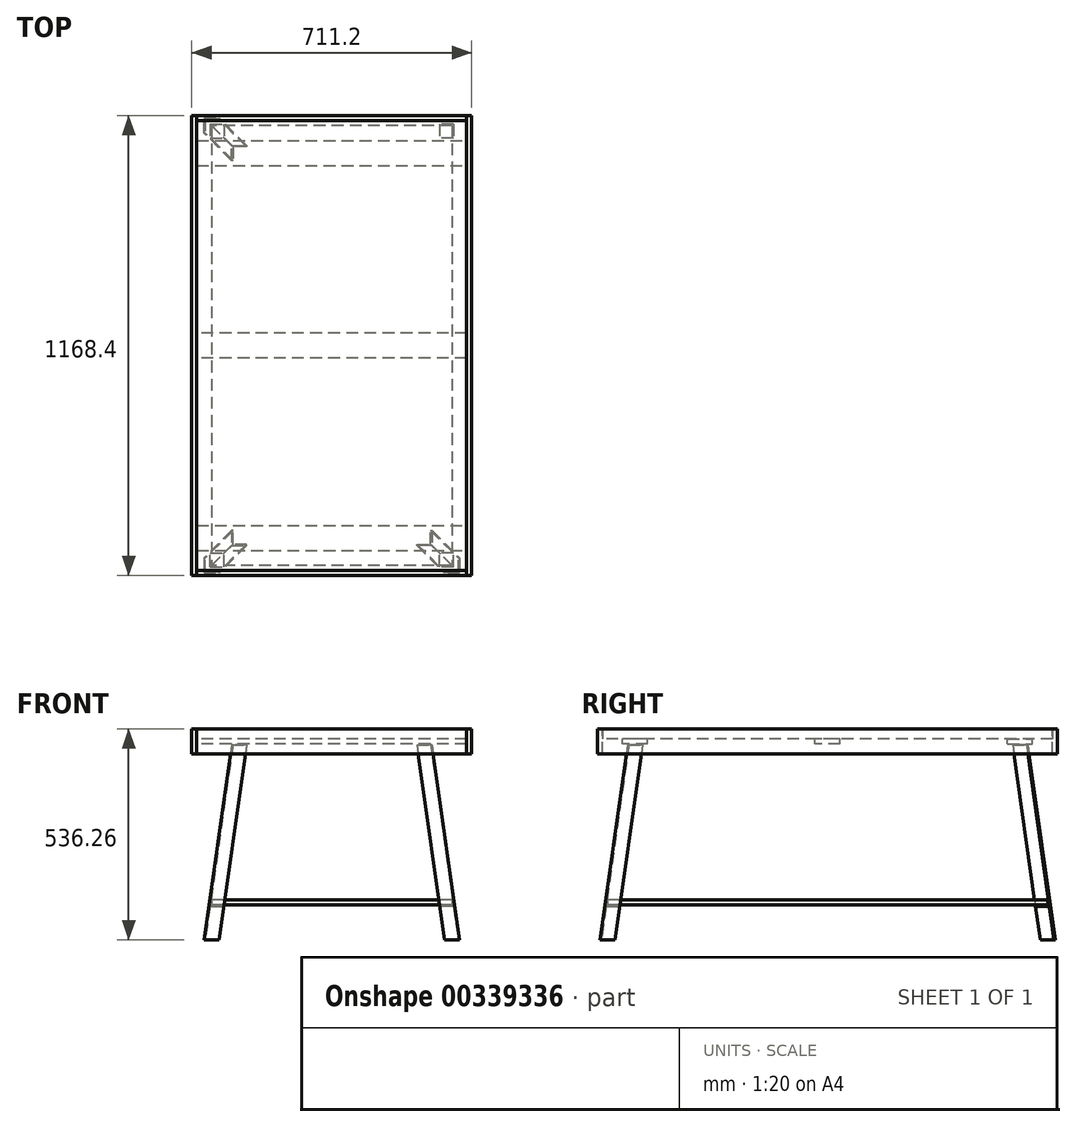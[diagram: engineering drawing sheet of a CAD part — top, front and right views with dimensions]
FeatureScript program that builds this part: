
annotation { "Feature Type Name" : "Feature", "Feature Type Description" : "" }
export const myFeature = defineFeature(function(context is Context, id is Id, definition is map)
    precondition{}
    {
        {
            var Q0;
            Q0=qCreatedBy(makeId("Top.planeOp"),FACE);
            var sketch = newSketch(context, id + "F0", { "sketchPlane" : qUnion([Q0])});
            skLineSegment(sketch, "E0.bottom", {"start": v(342.9, 571.5) * mm, "end": v(-342.9, 571.5) * mm});
            skLineSegment(sketch, "E0.top", {"start": v(342.9, -571.5) * mm, "end": v(-342.9, -571.5) * mm});
            skLineSegment(sketch, "E0.left", {"start": v(342.9, 571.5) * mm, "end": v(342.9, -571.5) * mm});
            skLineSegment(sketch, "E0.right", {"start": v(-342.9, 571.5) * mm, "end": v(-342.9, -571.5) * mm});
            skPoint(sketch, "E0.middle", {"position": v(0, 0) * mm});
            skSolve(sketch);
        }
        {
            var Q0;
            Q0=qSketchRegion(id+"F0",true);
            extrude(context, id + "F1", {"entities" : qUnion([Q0]), "depth" : 25.4 * mm});
        }
        {
            var Q0;
            Q0=makeQuery(id+"F1.opExtrude","CAP_FACE",FACE,{"disambiguationData":[OSD([sQuery(id+"F0.wireOp",EDGE,"E0.bottom"),sQuery(id+"F0.wireOp",EDGE,"E0.top"),sQuery(id+"F0.wireOp",EDGE,"E0.left"),sQuery(id+"F0.wireOp",EDGE,"E0.right")])],"isStart":false});
            var sketch = newSketch(context, id + "F2", { "sketchPlane" : qUnion([Q0])});
            skLineSegment(sketch, "E1.bottom", {"start": v(-342.9, -571.5) * mm, "end": v(342.9, -571.5) * mm});
            skLineSegment(sketch, "E1.top", {"start": v(-342.9, -584.2) * mm, "end": v(342.9, -584.2) * mm});
            skLineSegment(sketch, "E1.left", {"start": v(-342.9, -571.5) * mm, "end": v(-342.9, -584.2) * mm});
            skLineSegment(sketch, "E1.right", {"start": v(342.9, -571.5) * mm, "end": v(342.9, -584.2) * mm});
            skLineSegment(sketch, "E2.bottom", {"start": v(-342.9, -584.2) * mm, "end": v(-355.6, -584.2) * mm});
            skLineSegment(sketch, "E2.top", {"start": v(-342.9, 584.2) * mm, "end": v(-355.6, 584.2) * mm});
            skLineSegment(sketch, "E2.left", {"start": v(-342.9, -584.2) * mm, "end": v(-342.9, 584.2) * mm});
            skLineSegment(sketch, "E2.right", {"start": v(-355.6, -584.2) * mm, "end": v(-355.6, 584.2) * mm});
            skSolve(sketch);
        }
        {
            var Q0;
            {var subQ0=sQuery(id+"F2.wireOp",EDGE,"E1.bottom");Q0=makeQuery(id+"F2.imprint","IMPRINT",FACE,{"disambiguationData":[TD([[makeQuery(id+"F2.imprint","IMPRINT",EDGE,{"derivedFrom":subQ0}),1.0]])]});}
            extrude(context, id + "F3", {"entities" : qUnion([Q0]), "oppositeDirection" : true, "depth" : 63.5 * mm});
        }
        {
            var Q0;
            {var subQ3=sQuery(id+"F2.wireOp",EDGE,"E2.bottom");Q0=makeQuery(id+"F2.imprint","IMPRINT",FACE,{"disambiguationData":[TD([[makeQuery(id+"F2.imprint","IMPRINT",EDGE,{"derivedFrom":subQ3}),-1.0]])]});}
            extrude(context, id + "F4", {"entities" : qUnion([Q0]), "oppositeDirection" : true, "depth" : 63.5 * mm});
        }
        {
            var Q0;
            Q0=makeQuery(id+"F4.opExtrude","SWEPT_BODY",BODY,{"disambiguationData":[OSD([sQuery(id+"F2.wireOp",EDGE,"E2.bottom"),sQuery(id+"F2.wireOp",EDGE,"E2.top"),sQuery(id+"F2.wireOp",EDGE,"E2.left"),sQuery(id+"F2.wireOp",EDGE,"E2.right")])]});
            var Q1;
            Q1=qCreatedBy(makeId("Right.planeOp"),FACE);
            mirror(context, id + "F5", {"entities" : qUnion([Q0]), "mirrorPlane" : qUnion([Q1])});
        }
        {
            var Q0;
            Q0=makeQuery(id+"F3.opExtrude","SWEPT_BODY",BODY,{"disambiguationData":[OSD([sQuery(id+"F2.wireOp",EDGE,"E1.bottom"),sQuery(id+"F2.wireOp",EDGE,"E1.top"),sQuery(id+"F2.wireOp",EDGE,"E1.right"),sQuery(id+"F2.wireOp",EDGE,"E2.left")])]});
            var Q1;
            Q1=qCreatedBy(makeId("Front.planeOp"),FACE);
            mirror(context, id + "F6", {"entities" : qUnion([Q0]), "mirrorPlane" : qUnion([Q1])});
        }
        {
            var Q0;
            Q0=makeQuery(id+"F1.opExtrude","CAP_FACE",FACE,{"disambiguationData":[OSD([sQuery(id+"F0.wireOp",EDGE,"E0.bottom"),sQuery(id+"F0.wireOp",EDGE,"E0.top"),sQuery(id+"F0.wireOp",EDGE,"E0.left"),sQuery(id+"F0.wireOp",EDGE,"E0.right")])],"isStart":true});
            var sketch = newSketch(context, id + "F7", { "sketchPlane" : qUnion([Q0])});
            skLineSegment(sketch, "E3.bottom", {"start": v(-342.9, 520.7) * mm, "end": v(342.9, 520.7) * mm});
            skLineSegment(sketch, "E3.top", {"start": v(-342.9, 457.2) * mm, "end": v(342.9, 457.2) * mm});
            skLineSegment(sketch, "E3.left", {"start": v(-342.9, 520.7) * mm, "end": v(-342.9, 457.2) * mm});
            skLineSegment(sketch, "E3.right", {"start": v(342.9, 520.7) * mm, "end": v(342.9, 457.2) * mm});
            skLineSegment(sketch, "E4.bottom", {"start": v(342.9, -31.75) * mm, "end": v(-342.9, -31.75) * mm});
            skLineSegment(sketch, "E4.top", {"start": v(342.9, 31.75) * mm, "end": v(-342.9, 31.75) * mm});
            skLineSegment(sketch, "E4.left", {"start": v(342.9, -31.75) * mm, "end": v(342.9, 31.75) * mm});
            skLineSegment(sketch, "E4.right", {"start": v(-342.9, -31.75) * mm, "end": v(-342.9, 31.75) * mm});
            skPoint(sketch, "E4.middle", {"position": v(0, 0) * mm});
            skSolve(sketch);
        }
        {
            var Q0;
            Q0=qSketchRegion(id+"F7",true);
            extrude(context, id + "F8", {"entities" : qUnion([Q0]), "depth" : 12.7 * mm});
        }
        {
            var Q0;
            Q0=makeQuery(id+"F8.opExtrude","CAP_FACE",FACE,{"disambiguationData":[OSD([sQuery(id+"F7.wireOp",EDGE,"E3.bottom"),sQuery(id+"F7.wireOp",EDGE,"E3.top"),sQuery(id+"F7.wireOp",EDGE,"E3.left"),sQuery(id+"F7.wireOp",EDGE,"E3.right")])],"isStart":false});
            var sketch = newSketch(context, id + "F9", { "sketchPlane" : qUnion([Q0])});
            skLineSegment(sketch, "E5", {"start": v(-254, 469.9) * mm, "end": v(-254, 508) * mm});
            skLineSegment(sketch, "E6", {"start": v(-254, 508) * mm, "end": v(-215.9, 508) * mm});
            skLineSegment(sketch, "E7", {"start": v(-215.9, 508) * mm, "end": v(-215.9, 504.82) * mm});
            skLineSegment(sketch, "E8", {"start": v(-215.9, 504.82) * mm, "end": v(-250.83, 504.82) * mm});
            skLineSegment(sketch, "E9", {"start": v(-250.83, 504.82) * mm, "end": v(-250.83, 469.9) * mm});
            skLineSegment(sketch, "E10", {"start": v(-250.83, 469.9) * mm, "end": v(-254, 469.9) * mm});
            skLineSegment(sketch, "E11", {"start": v(-254, 488.95) * mm, "end": v(-342.9, 488.95) * mm, "construction": true});
            skSolve(sketch);
        }
        {
            var Q0;
            Q0=sQuery(id+"F9.wireOp",EDGE,"E6");
            var Q1;
            Q1=makeQuery(id+"F9.imprint","IMPRINT",FACE,{"disambiguationData":[TD([[makeQuery(id+"F9.imprint","IMPRINT",EDGE,{"derivedFrom":sQuery(id+"F9.wireOp",EDGE,"E5")}),1.0]])]});
            cPlane(context, id + "F10", {"entities" : qUnion([Q0, Q1]), "cplaneType" : CPlaneType.LINE_ANGLE, "offset" : 25.4 * mm, "angle" : 82 * degree, "width" : 152.4 * mm, "height" : 152.4 * mm});
        }
        {
            var Q0;
            Q0=qCreatedBy(id+"F10.planeOp",FACE);
            var sketch = newSketch(context, id + "F11", { "sketchPlane" : qUnion([Q0])});
            skLineSegment(sketch, "E12", {"start": v(-254, -83.28) * mm, "end": v(-324.7, -586.33) * mm});
            skLineSegment(sketch, "E13", {"start": v(-254, -83.28) * mm, "end": v(-254, -459.38) * mm, "construction": true});
            skSolve(sketch);
        }
        {
            var Q0;
            Q0=makeQuery(id+"F9.imprint","IMPRINT",FACE,{"disambiguationData":[TD([[makeQuery(id+"F9.imprint","IMPRINT",EDGE,{"derivedFrom":sQuery(id+"F9.wireOp",EDGE,"E5")}),-1.0]])]});
            var Q1;
            Q1=sQuery(id+"F11.wireOp",EDGE,"E12");
            sweep(context, id + "F12", {"profiles" : qUnion([Q0]), "path" : qUnion([Q1])});
        }
        {
            var Q0;
            Q0=makeQuery(id+"F8.opExtrude","CAP_FACE",FACE,{"disambiguationData":[OSD([sQuery(id+"F7.wireOp",EDGE,"E3.bottom"),sQuery(id+"F7.wireOp",EDGE,"E3.top"),sQuery(id+"F7.wireOp",EDGE,"E3.left"),sQuery(id+"F7.wireOp",EDGE,"E3.right")])],"isStart":false});
            var sketch = newSketch(context, id + "F13", { "sketchPlane" : qUnion([Q0])});
            skLineSegment(sketch, "E14.bottom", {"start": v(304.8, 514.35) * mm, "end": v(-304.8, 514.35) * mm});
            skLineSegment(sketch, "E14.top", {"start": v(304.8, 463.55) * mm, "end": v(-304.8, 463.55) * mm});
            skLineSegment(sketch, "E14.left", {"start": v(304.8, 514.35) * mm, "end": v(304.8, 463.55) * mm});
            skLineSegment(sketch, "E14.right", {"start": v(-304.8, 514.35) * mm, "end": v(-304.8, 463.55) * mm});
            skLineSegment(sketch, "E15", {"start": v(0, 463.55) * mm, "end": v(0, 0) * mm, "construction": true});
            skLineSegment(sketch, "E16", {"start": v(342.9, 488.95) * mm, "end": v(304.8, 488.95) * mm, "construction": true});
            skPoint(sketch, "E16.endSnap0", {"position": v(304.8, 488.95) * mm});
            skSolve(sketch);
        }
        {
            var Q0;
            Q0=qSketchRegion(id+"F13",true);
            extrude(context, id + "F14", {"entities" : qUnion([Q0]), "depth" : 3.17 * mm});
        }
        {
            var Q0;
            Q0=qSketchRegion(id+"F13",true);
            extrude(context, id + "F15", {"entities" : qUnion([Q0]), "operationType" : NewBodyOperationType.REMOVE, "depth" : 3.17 * mm});
        }
        {
            var Q0;
            Q0=makeQuery(id+"F12.opSweep","SWEPT_BODY",BODY,{"disambiguationData":[OSD([sQuery(id+"F9.wireOp",EDGE,"E5"),sQuery(id+"F9.wireOp",EDGE,"E6"),sQuery(id+"F9.wireOp",EDGE,"E7"),sQuery(id+"F9.wireOp",EDGE,"E8"),sQuery(id+"F9.wireOp",EDGE,"E9"),sQuery(id+"F9.wireOp",EDGE,"E10"),sQuery(id+"F11.wireOp",EDGE,"E12")])]});
            var Q1;
            Q1=qCreatedBy(makeId("Right.planeOp"),FACE);
            mirror(context, id + "F16", {"operationType" : NewBodyOperationType.ADD, "entities" : qUnion([Q0]), "mirrorPlane" : qUnion([Q1])});
        }
        {
            var Q0;
            Q0=makeQuery(id+"F16.opPattern","COPY",FACE,{"derivedFrom":makeQuery(id+"F12.opSweep","SWEPT_FACE",FACE,{"disambiguationData":[OSD([sQuery(id+"F9.wireOp",EDGE,"E8"),sQuery(id+"F11.wireOp",EDGE,"E12")])]}),"instanceName":"1"});
            var sketch = newSketch(context, id + "F17", { "sketchPlane" : qUnion([Q0])});
            skLineSegment(sketch, "E17", {"start": v(-263.65, -174.08) * mm, "end": v(297.1, -412.1) * mm});
            skLineSegment(sketch, "E18", {"start": v(297.1, -412.1) * mm, "end": v(301.08, -440.44) * mm});
            skLineSegment(sketch, "E19", {"start": v(301.08, -440.44) * mm, "end": v(-267.18, -199.23) * mm});
            skLineSegment(sketch, "E20", {"start": v(-267.18, -199.23) * mm, "end": v(-263.65, -174.08) * mm});
            skSolve(sketch);
        }
        {
            var Q0;
            Q0=qSketchRegion(id+"F17",true);
            extrude(context, id + "F18", {"entities" : qUnion([Q0]), "depth" : 3.17 * mm});
        }
        {
            var Q0;
            Q0=makeQuery(id+"F18.opExtrude","SWEPT_BODY",BODY,{"disambiguationData":[OSD([sQuery(id+"F17.wireOp",EDGE,"E17"),sQuery(id+"F17.wireOp",EDGE,"E18"),sQuery(id+"F17.wireOp",EDGE,"E19"),sQuery(id+"F17.wireOp",EDGE,"E20")])]});
            var Q1;
            Q1=qCreatedBy(makeId("Right.planeOp"),FACE);
            mirror(context, id + "F19", {"entities" : qUnion([Q0]), "mirrorPlane" : qUnion([Q1])});
        }
        {
            var Q0;
            Q0=makeQuery(id+"F16.opPattern","COPY",FACE,{"derivedFrom":makeQuery(id+"F12.opSweep","CAP_FACE",FACE,{"disambiguationData":[OSD([sQuery(id+"F9.wireOp",EDGE,"E5"),sQuery(id+"F9.wireOp",EDGE,"E6"),sQuery(id+"F9.wireOp",EDGE,"E7"),sQuery(id+"F9.wireOp",EDGE,"E8"),sQuery(id+"F9.wireOp",EDGE,"E9"),sQuery(id+"F9.wireOp",EDGE,"E10"),sQuery(id+"F11.wireOp",VERTEX,"E12.end")])],"isStart":false}),"instanceName":"1"});
            cPlane(context, id + "F20", {"entities" : qUnion([Q0]), "cplaneType" : CPlaneType.OFFSET, "offset" : 88.9 * mm, "oppositeDirection" : true, "width" : 152.4 * mm, "height" : 152.4 * mm});
        }
        {
            var Q0;
            Q0=qCreatedBy(id+"F20.planeOp",FACE);
            var sketch = newSketch(context, id + "F21", { "sketchPlane" : qUnion([Q0])});
            skLineSegment(sketch, "E21.bottom", {"start": v(308.9, 562.34) * mm, "end": v(273.98, 562.34) * mm});
            skLineSegment(sketch, "E21.top", {"start": v(308.9, 527.42) * mm, "end": v(273.98, 527.42) * mm});
            skLineSegment(sketch, "E21.left", {"start": v(308.9, 562.34) * mm, "end": v(308.9, 527.42) * mm});
            skLineSegment(sketch, "E21.right", {"start": v(273.98, 562.34) * mm, "end": v(273.98, 527.42) * mm});
            skSolve(sketch);
        }
        {
            var Q0;
            Q0=qSketchRegion(id+"F21",true);
            extrude(context, id + "F22", {"entities" : qUnion([Q0]), "depth" : 3.17 * mm});
        }
        {
            var Q0;
            Q0=makeQuery(id+"F22.opExtrude","SWEPT_BODY",BODY,{"disambiguationData":[OSD([sQuery(id+"F21.wireOp",EDGE,"E21.bottom"),sQuery(id+"F21.wireOp",EDGE,"E21.top"),sQuery(id+"F21.wireOp",EDGE,"E21.left"),sQuery(id+"F21.wireOp",EDGE,"E21.right")])]});
            var Q1;
            Q1=qCreatedBy(makeId("Right.planeOp"),FACE);
            mirror(context, id + "F23", {"entities" : qUnion([Q0]), "mirrorPlane" : qUnion([Q1])});
        }
        {
            var Q0;
            Q0=makeQuery(id+"F8.opExtrude","SWEPT_BODY",BODY,{"disambiguationData":[OSD([sQuery(id+"F7.wireOp",EDGE,"E3.bottom"),sQuery(id+"F7.wireOp",EDGE,"E3.top"),sQuery(id+"F7.wireOp",EDGE,"E3.left"),sQuery(id+"F7.wireOp",EDGE,"E3.right")])]});
            var Q1;
            Q1=makeQuery(id+"F12.opSweep","SWEPT_BODY",BODY,{"disambiguationData":[OSD([sQuery(id+"F9.wireOp",EDGE,"E5"),sQuery(id+"F9.wireOp",EDGE,"E6"),sQuery(id+"F9.wireOp",EDGE,"E7"),sQuery(id+"F9.wireOp",EDGE,"E8"),sQuery(id+"F9.wireOp",EDGE,"E9"),sQuery(id+"F9.wireOp",EDGE,"E10"),sQuery(id+"F11.wireOp",EDGE,"E12")])]});
            var Q2;
            Q2=makeQuery(id+"F19.opPattern","COPY",BODY,{"derivedFrom":makeQuery(id+"F18.opExtrude","SWEPT_BODY",BODY,{"disambiguationData":[OSD([sQuery(id+"F17.wireOp",EDGE,"E17"),sQuery(id+"F17.wireOp",EDGE,"E18"),sQuery(id+"F17.wireOp",EDGE,"E19"),sQuery(id+"F17.wireOp",EDGE,"E20")])]}),"instanceName":"1"});
            var Q3;
            Q3=makeQuery(id+"F18.opExtrude","SWEPT_BODY",BODY,{"disambiguationData":[OSD([sQuery(id+"F17.wireOp",EDGE,"E17"),sQuery(id+"F17.wireOp",EDGE,"E18"),sQuery(id+"F17.wireOp",EDGE,"E19"),sQuery(id+"F17.wireOp",EDGE,"E20")])]});
            var Q4;
            Q4=makeQuery(id+"F23.opPattern","COPY",BODY,{"derivedFrom":makeQuery(id+"F22.opExtrude","SWEPT_BODY",BODY,{"disambiguationData":[OSD([sQuery(id+"F21.wireOp",EDGE,"E21.bottom"),sQuery(id+"F21.wireOp",EDGE,"E21.top"),sQuery(id+"F21.wireOp",EDGE,"E21.left"),sQuery(id+"F21.wireOp",EDGE,"E21.right")])]}),"instanceName":"1"});
            var Q5;
            Q5=makeQuery(id+"F22.opExtrude","SWEPT_BODY",BODY,{"disambiguationData":[OSD([sQuery(id+"F21.wireOp",EDGE,"E21.bottom"),sQuery(id+"F21.wireOp",EDGE,"E21.top"),sQuery(id+"F21.wireOp",EDGE,"E21.left"),sQuery(id+"F21.wireOp",EDGE,"E21.right")])]});
            var Q6;
            Q6=qCreatedBy(makeId("Front.planeOp"),FACE);
            mirror(context, id + "F24", {"entities" : qUnion([Q0, Q1, Q2, Q3, Q4, Q5]), "mirrorPlane" : qUnion([Q6])});
        }
        {
            var Q0;
            Q0=makeQuery(id+"F22.opExtrude","CAP_FACE",FACE,{"disambiguationData":[OSD([sQuery(id+"F21.wireOp",EDGE,"E21.bottom"),sQuery(id+"F21.wireOp",EDGE,"E21.top"),sQuery(id+"F21.wireOp",EDGE,"E21.left"),sQuery(id+"F21.wireOp",EDGE,"E21.right")])],"isStart":true});
            var sketch = newSketch(context, id + "F25", { "sketchPlane" : qUnion([Q0])});
            skLineSegment(sketch, "E22.bottom", {"start": v(305.73, 559.17) * mm, "end": v(-305.73, 559.17) * mm});
            skLineSegment(sketch, "E22.top", {"start": v(305.73, -559.17) * mm, "end": v(-305.73, -559.17) * mm});
            skLineSegment(sketch, "E22.left", {"start": v(305.73, 559.17) * mm, "end": v(305.73, -559.17) * mm});
            skLineSegment(sketch, "E22.right", {"start": v(-305.73, 559.17) * mm, "end": v(-305.73, -559.17) * mm});
            skSolve(sketch);
        }
        {
            var Q0;
            Q0=qSketchRegion(id+"F25",true);
            extrude(context, id + "F26", {"entities" : qUnion([Q0]), "depth" : 12.7 * mm});
        }
        {
            var Q0;
            Q0=makeQuery(id+"F19.opPattern","COPY",BODY,{"derivedFrom":makeQuery(id+"F18.opExtrude","SWEPT_BODY",BODY,{"disambiguationData":[OSD([sQuery(id+"F17.wireOp",EDGE,"E17"),sQuery(id+"F17.wireOp",EDGE,"E18"),sQuery(id+"F17.wireOp",EDGE,"E19"),sQuery(id+"F17.wireOp",EDGE,"E20")])]}),"instanceName":"1"});
            var Q1;
            Q1=makeQuery(id+"F18.opExtrude","SWEPT_BODY",BODY,{"disambiguationData":[OSD([sQuery(id+"F17.wireOp",EDGE,"E17"),sQuery(id+"F17.wireOp",EDGE,"E18"),sQuery(id+"F17.wireOp",EDGE,"E19"),sQuery(id+"F17.wireOp",EDGE,"E20")])]});
            var Q2;
            Q2=makeQuery(id+"F24.opPattern","COPY",BODY,{"derivedFrom":makeQuery(id+"F18.opExtrude","SWEPT_BODY",BODY,{"disambiguationData":[OSD([sQuery(id+"F17.wireOp",EDGE,"E17"),sQuery(id+"F17.wireOp",EDGE,"E18"),sQuery(id+"F17.wireOp",EDGE,"E19"),sQuery(id+"F17.wireOp",EDGE,"E20")])]}),"instanceName":"1"});
            var Q3;
            Q3=makeQuery(id+"F24.opPattern","COPY",BODY,{"derivedFrom":makeQuery(id+"F19.opPattern","COPY",BODY,{"derivedFrom":makeQuery(id+"F18.opExtrude","SWEPT_BODY",BODY,{"disambiguationData":[OSD([sQuery(id+"F17.wireOp",EDGE,"E17"),sQuery(id+"F17.wireOp",EDGE,"E18"),sQuery(id+"F17.wireOp",EDGE,"E19"),sQuery(id+"F17.wireOp",EDGE,"E20")])]}),"instanceName":"1"}),"instanceName":"1"});
            deleteBodies(context, id + "F27", {"entities" : qUnion([Q0, Q1, Q2, Q3])});
        }
    });
